# Revit family: 0047059
name_source: partatom
category: Lighting Fixtures
revit_build: Autodesk Revit 2016 (Build: 20150220_1215(x64)
units: mm (PartAtom-declared; Revit-internal decimal feet)

## family parameters
Cut with Voids When Loaded = No
Host = Face
Light Source = Yes
OmniClass Number = 23.80.70.00
OmniClass Title = Lighting
Part Type = Normal
Room Calculation Point = No
Round Connector Dimension = Use Diameter
Shared = No

## types (1)
- 0047059 ST SRF WLL R IP54 465LM 840 BLK
    Apparent Load = 7 VA
    Assembly Code = D5020200
    AssetType = Fixed
    ClassificationName = Uniclass2015
    ClassificationValue = EF_70_80
    Color Filter = 16777215
    Cost = 0 $
    Default Elevation = 1219 mm
    Dimming Lamp Color Temperature Shift = <None>
    DocumentationLiterature = http://www.sylvania-lighting.com
    ElectricShockClassification = Class I
    Emit Shape Visible in Rendering = No
    Emit from Circle Diameter = 45 mm  [stored 0.147638 ft]
    IfcExportAs = IfcLightFixtureType
    IfcExportType = IfcLightFixtureType
    ImpactProtectionIndex = IK07
    IngressProtection = IP54
    Keynote = 16500
    Lamp = LED
    LampColourRenderingIndex = 80
    LampColourTemperature = 3000 K
    LampMacAdamStep = 6
    LampNominalLuminous = 465 lm
    LampsType = LED
    LuminousEfficacy = 66 lm/W
    Manufacturer = Feilo Sylvania
    ManufacturerName = Feilo Sylvania
    Material = aluminum housing, glass diffuser
    Material_1_SYL = Body-Sylvania-STARTSurfaceWall
    Material_2_SYL = LED-Sylvania
    Material_3_SYL = Lens-Sylvania
    Material_4_SYL = Reflector-Sylvania
    Model = START Surface Wall Round IP54 465lm 840 BLK
    ModelNumber = 0047059
    ModelReference = START Surface Wall Round IP54 465lm 840 BLK
    Name = START Surface Wall Round IP54 465lm 840 BLK
    NominalDepth = 99 mm  [stored 0.324803 ft]
    NominalHeight = 65 mm  [stored 0.213255 ft]
    NominalLength = 135 mm  [stored 0.442913 ft]
    Photometric Web File = 0047059.ies
    PowerConsumption = 7 W
    PowerFactor = 0.82
    Tilt Angle = -90.00°
    Type Image = <None>
    TypeName = START Surface Wall Round IP54 465lm 840 BLK
    URL = http://www.sylvania-lighting.com
    Voltage = 230 V
    Weight = 8.0 kg

note: [stored X ft] marks values corroborated as IEEE doubles in the binary element streams (Revit-internal decimal feet)

## geometry (parser evidence)
native form markers: Sweep x2
no freeform markers — native parametric forms only
